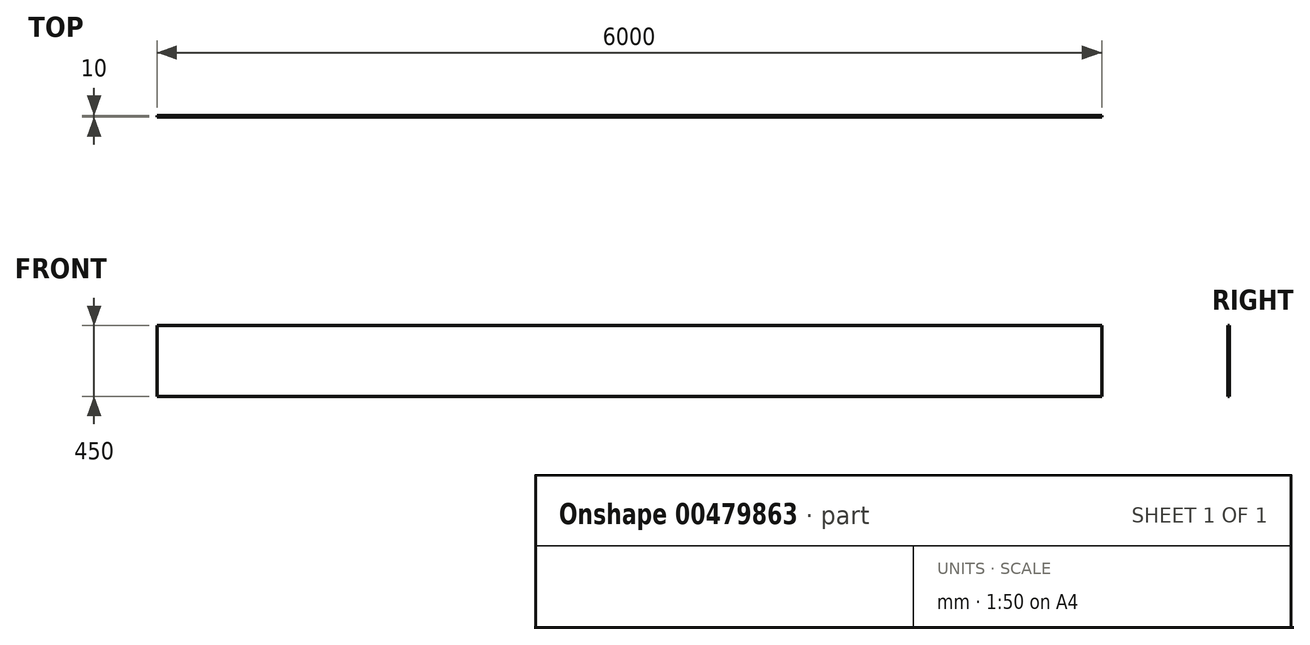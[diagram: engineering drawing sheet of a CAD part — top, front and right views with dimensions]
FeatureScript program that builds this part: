
annotation { "Feature Type Name" : "Feature", "Feature Type Description" : "" }
export const myFeature = defineFeature(function(context is Context, id is Id, definition is map)
    precondition{}
    {
        {
            var Q0;
            Q0=qCreatedBy(makeId("Front.planeOp"),FACE);
            var sketch = newSketch(context, id + "F0", { "sketchPlane" : qUnion([Q0])});
            skLineSegment(sketch, "E0.bottom", {"start": v(-1960.8, 274.79) * mm, "end": v(4039.2, 274.79) * mm});
            skLineSegment(sketch, "E0.top", {"start": v(-1960.8, -175.21) * mm, "end": v(4039.2, -175.21) * mm});
            skLineSegment(sketch, "E0.left", {"start": v(-1960.8, 274.79) * mm, "end": v(-1960.8, -175.21) * mm});
            skLineSegment(sketch, "E0.right", {"start": v(4039.2, 274.79) * mm, "end": v(4039.2, -175.21) * mm});
            skSolve(sketch);
        }
        {
            var Q0;
            Q0=makeQuery(id+"F0.imprint","IMPRINT",FACE,{"disambiguationData":[TD([[makeQuery(id+"F0.imprint","IMPRINT",EDGE,{"derivedFrom":sQuery(id+"F0.wireOp",EDGE,"E0.bottom")}),-1.0]])]});
            extrude(context, id + "F1", {"entities" : qUnion([Q0]), "depth" : 10 * mm});
        }
    });
